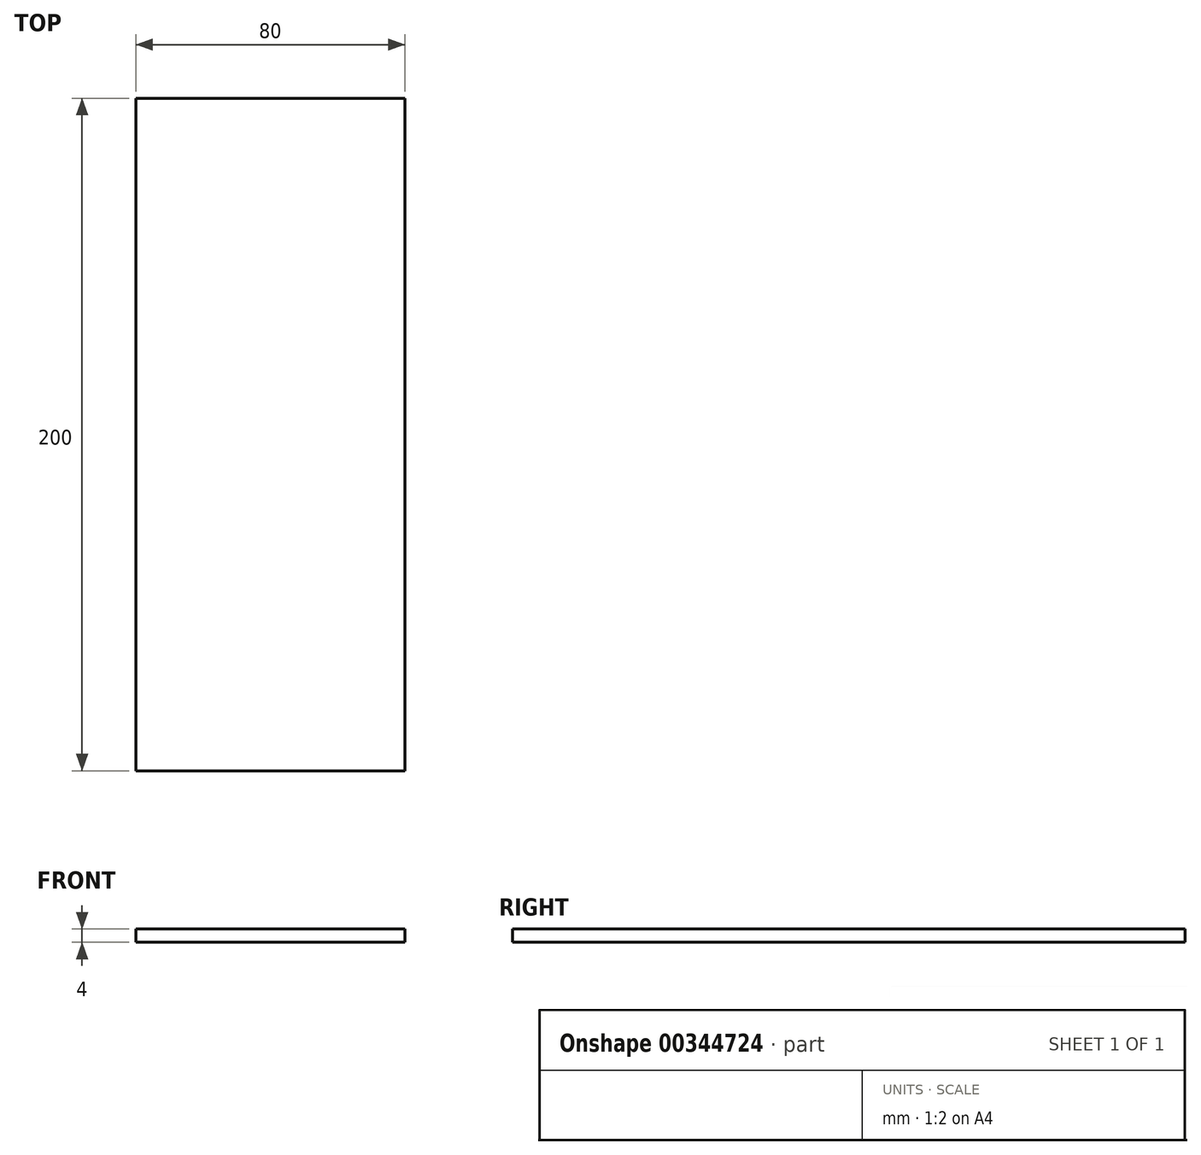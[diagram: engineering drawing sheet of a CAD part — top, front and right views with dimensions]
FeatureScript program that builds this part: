
annotation { "Feature Type Name" : "Feature", "Feature Type Description" : "" }
export const myFeature = defineFeature(function(context is Context, id is Id, definition is map)
    precondition{}
    {
        {
            var Q0;
            Q0=qCreatedBy(makeId("Top.planeOp"),FACE);
            var sketch = newSketch(context, id + "F0", { "sketchPlane" : qUnion([Q0])});
            skLineSegment(sketch, "E0.bottom", {"start": v(0, 0) * mm, "end": v(80, 0) * mm});
            skLineSegment(sketch, "E0.top", {"start": v(0, 200) * mm, "end": v(80, 200) * mm});
            skLineSegment(sketch, "E0.left", {"start": v(0, 0) * mm, "end": v(0, 200) * mm});
            skLineSegment(sketch, "E0.right", {"start": v(80, 0) * mm, "end": v(80, 200) * mm});
            skSolve(sketch);
        }
        {
            var Q0;
            Q0=makeQuery(id+"F0.imprint","IMPRINT",FACE,{"disambiguationData":[TD([[makeQuery(id+"F0.imprint","IMPRINT",EDGE,{"derivedFrom":sQuery(id+"F0.wireOp",EDGE,"E0.bottom")}),1.0]])]});
            extrude(context, id + "F1", {"entities" : qUnion([Q0]), "depth" : 4 * mm});
        }
    });
